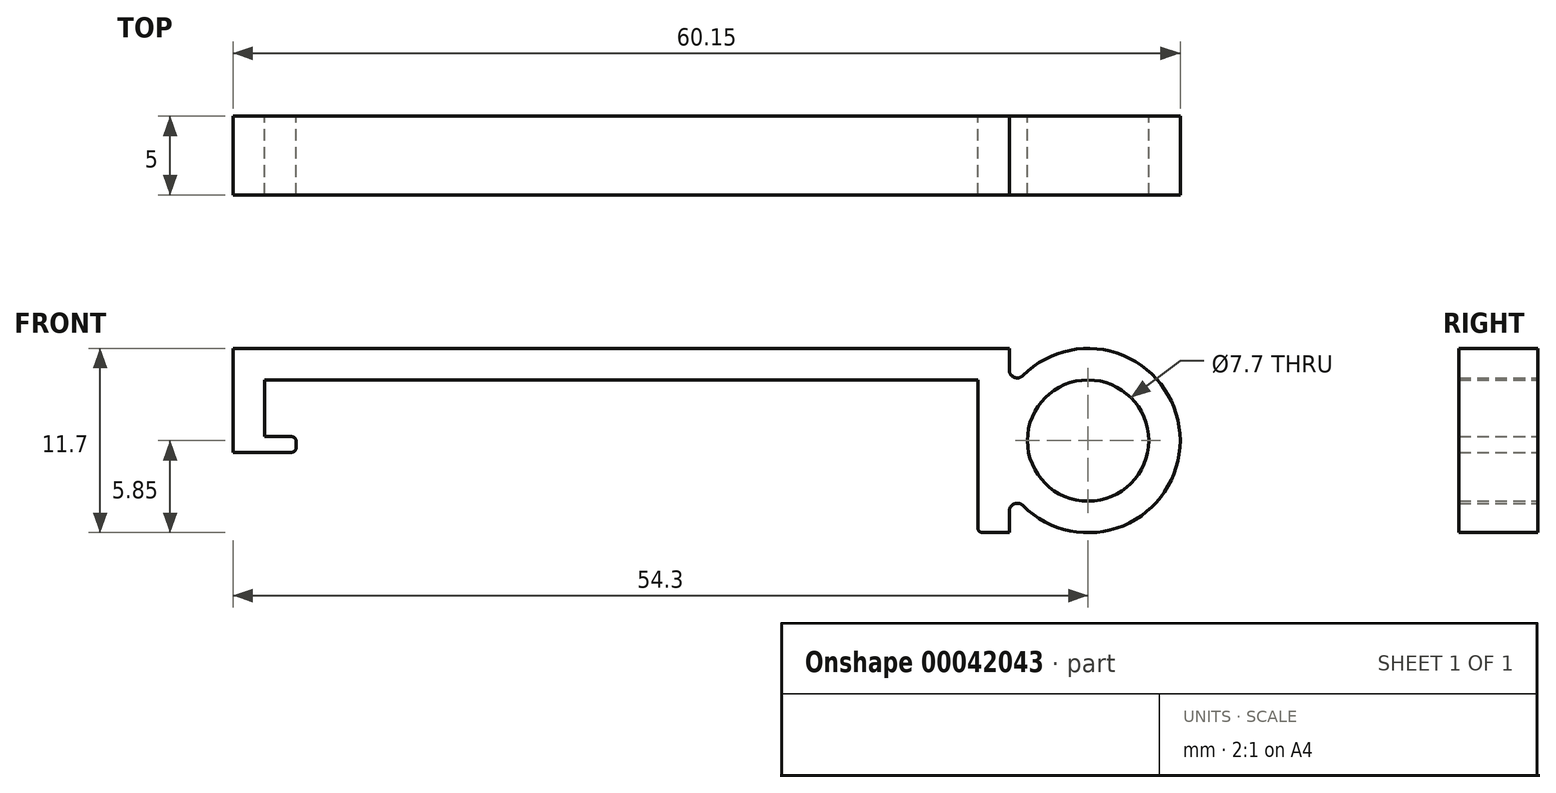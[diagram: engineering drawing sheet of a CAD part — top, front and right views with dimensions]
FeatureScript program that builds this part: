
annotation { "Feature Type Name" : "Feature", "Feature Type Description" : "" }
export const myFeature = defineFeature(function(context is Context, id is Id, definition is map)
    precondition{}
    {
        {
            var Q0;
            Q0=qCreatedBy(makeId("Front.planeOp"),FACE);
            var sketch = newSketch(context, id + "F0", { "sketchPlane" : qUnion([Q0])});
            skLineSegment(sketch, "E0", {"start": v(22.65, 0) * mm, "end": v(-22.65, 0) * mm});
            skLineSegment(sketch, "E1", {"start": v(-22.65, 0) * mm, "end": v(-22.65, -3.6) * mm});
            skLineSegment(sketch, "E2", {"start": v(-24.65, -3.47) * mm, "end": v(-24.65, 2) * mm});
            skLineSegment(sketch, "E3", {"start": v(-24.65, 2) * mm, "end": v(24.65, 2) * mm});
            skLineSegment(sketch, "E4", {"start": v(24.65, 2) * mm, "end": v(24.65, 0.63) * mm});
            skLineSegment(sketch, "E5", {"start": v(24.65, -9.7) * mm, "end": v(22.65, -9.7) * mm});
            skLineSegment(sketch, "E6", {"start": v(22.65, -9.7) * mm, "end": v(22.65, 0) * mm});
            skArc(sketch, "E7", {"start": v(25.5, -7.98) * mm, "mid": v(35.5, -3.85) * mm, "end": v(25.5, 0.28) * mm});
            skPoint(sketch, "E8", {"position": v(0, 0) * mm});
            skCircle(sketch, "E9", {"center": v(29.65, -3.85) * mm, "radius": 3.85 * mm});
            skLineSegment(sketch, "E10", {"start": v(33.5, -3.85) * mm, "end": v(35.5, -3.85) * mm, "construction": true});
            skLineSegment(sketch, "E11.trimOffspring", {"start": v(24.65, -8.33) * mm, "end": v(24.65, -9.7) * mm});
            skPoint(sketch, "E12.visualSharp", {"position": v(24.65, -0.81) * mm});
            skArc(sketch, "E12.filletArc", {"start": v(24.65, 0.63) * mm, "mid": v(24.96, 0.17) * mm, "end": v(25.5, 0.28) * mm});
            skPoint(sketch, "E13.visualSharp", {"position": v(24.65, -6.89) * mm});
            skArc(sketch, "E13.filletArc", {"start": v(25.5, -7.98) * mm, "mid": v(24.96, -7.87) * mm, "end": v(24.65, -8.33) * mm});
            skLineSegment(sketch, "E14", {"start": v(-22.65, -3.6) * mm, "end": v(-20.65, -3.6) * mm});
            skLineSegment(sketch, "E15", {"start": v(-20.65, -3.6) * mm, "end": v(-20.65, -4.6) * mm});
            skLineSegment(sketch, "E16", {"start": v(-20.65, -4.6) * mm, "end": v(-24.65, -4.6) * mm});
            skLineSegment(sketch, "E17", {"start": v(-24.65, -4.6) * mm, "end": v(-24.65, -3.47) * mm});
            skPoint(sketch, "E18.end.orphan", {"position": v(-22.65, 2) * mm});
            skLineSegment(sketch, "E19", {"start": v(-22.65, 0) * mm, "end": v(-22.65, 2) * mm, "construction": true});
            skLineSegment(sketch, "E20", {"start": v(-22.65, 0) * mm, "end": v(-24.65, 0) * mm, "construction": true});
            skSolve(sketch);
        }
        {
            var Q0;
            Q0 = qSketchRegion(id + "F0", true);
            extrude(context, id + "F1", {"entities" : qUnion([Q0]), "depth" : 5 * mm});
        }
        {
            var Q0;
            Q0=makeQuery(id+"F1.opExtrude","SWEPT_EDGE",EDGE,{"disambiguationData":[OSD([sQuery(id+"F0.wireOp",EDGE,"E14"),sQuery(id+"F0.wireOp",EDGE,"E15")])]});
            var Q1;
            Q1=makeQuery(id+"F1.opExtrude","SWEPT_EDGE",EDGE,{"disambiguationData":[OSD([sQuery(id+"F0.wireOp",EDGE,"E15"),sQuery(id+"F0.wireOp",EDGE,"E16")])]});
            var Q2;
            Q2=makeQuery(id+"F1.opExtrude","SWEPT_EDGE",EDGE,{"disambiguationData":[OSD([sQuery(id+"F0.wireOp",EDGE,"E5"),sQuery(id+"F0.wireOp",EDGE,"E6")])]});
            fillet(context, id + "F2", {"entities" : qUnion([Q0, Q1, Q2]), "radius" : .3 * mm, "tangentPropagation" : true, "allowEdgeOverflow" : false});
        }
    });
